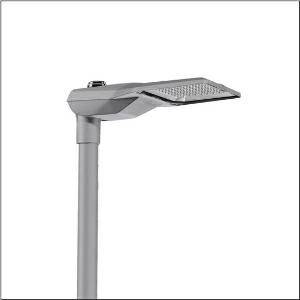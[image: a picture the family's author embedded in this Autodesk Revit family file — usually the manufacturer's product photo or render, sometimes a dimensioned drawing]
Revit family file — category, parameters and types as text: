
# Revit family: streetlight_sl_21_midi___st1_5a_5xe7p37n08mb_d4f4
name_source: partatom
category: Lighting Fixtures
units: mm (PartAtom-declared; Revit-internal decimal feet)

## family parameters
Cut with Voids When Loaded = No
Host = Face
Light Source = No
Part Type = Normal
Room Calculation Point = No
Round Connector Dimension = Use Diameter
Shared = No

## types (1)
- --- (1 x LED, 17960 lm, 136 W, 3000K)
    Apparent Load = 136 VA
    CIE Flux Codes = 22 53 95 100 100
    Color Rendering = 70
    Color Temperature = 3000K
    Default Elevation = 1800 mm
    Description = Streetlight SL 21 midi, mast luminaire, primary light control with lens, of PMMA, primary optical cover: cover, of toughened safety glass, transparent, light distribution: ST1.5a, light emission: direct distribution, primary light characteristic: asymmetric, installation type: side-entry, LED, 3G 2.5mm², High Power LED, rated luminous flux: 17.960lm, luminous efficacy: 132lm/W, light colour: 730, colour temperature: 3000K, control: overheat protection, pre-setting: linear dimming characteristic, constant luminous flux control, time-dependent luminous flux control, flexible luminous flux parameterisation, mains connection: 220..240V, AC, 50/60Hz, connection cable pre-assembled, cable length: 12,5m, wiring characteristics: H05VV-F, start of lifetime: 136W, end of service life: 142W, reduction: 61W, luminaire housing, of diecast aluminium (EN AC-44300), powder-coated, Siteco® metallic grey (DB 702S), corrosivity category C5 mid according to DIN EN ISO 12944, multi-level sealing system, sealing non-destructively replaceable, inclination adjustable: 0°, 5°, 10°, 15°, length: 644mm, width: 335mm, height: 110mm, spigot size: 42mm (side-entry), protection rating (complete): IP66, insulation class (complete): insulation class I (protective earthing), certification: CE, ENEC, ENEC+, VDE, impact resistance: IK09, permissible operating ambient temperature for outdoor applications: -40..+50°C, standard-compliant lighting for roads and squares, packaging unit: 1 piece

Light Distribution: ST1.5a
    Height = 111 mm
    Lamp = 1 x LED
    Lamp Light Flux = 17960 lm
    Lamp Power = 136 W
    Lamp count = 1
    Length = 644 mm
    Luminous efficacy = 132 lm/W
    Manufacturer = Siteco
    ModVariant = No
    Model = 5XE7P37N08MB
    Number of Poles = 1
    OnlyDefault = Yes
    Power Factor = 1
    Product Name = Streetlight SL 21 midi | ST1.5a
    Product group = mast luminaire | pylon top
    ProductGroupID = 6100
    Protection Class = Protection class I
    Protection Degree = IP 66
    RLX_Detail_Level = 1
    RLX_Emergency_Light_Flux = 0 lm
    RLX_Emergency_Type = 0
    RLX_Emergency_Type_DB = No
    RlxData = <blob elided: 94329 chars, md5=e50f132f>
    Socket = socket
    Standby Power = 0 W
    System Light Flux = 17960 lm
    System Power = 136 W
    Type Comments = factory setting: luminous flux: 100 % | dim-lin: 254 | 695 mA
    Type Image = l_1294377.jpg
    URL = http://relux.com
    VarID = @adj_103265
    Voltage = 0 V
    Weight = 0.00 kg
    Width = 336 mm

## geometry (parser evidence)
native form markers: Blend x4, Sweep x9
no freeform markers — native parametric forms only
